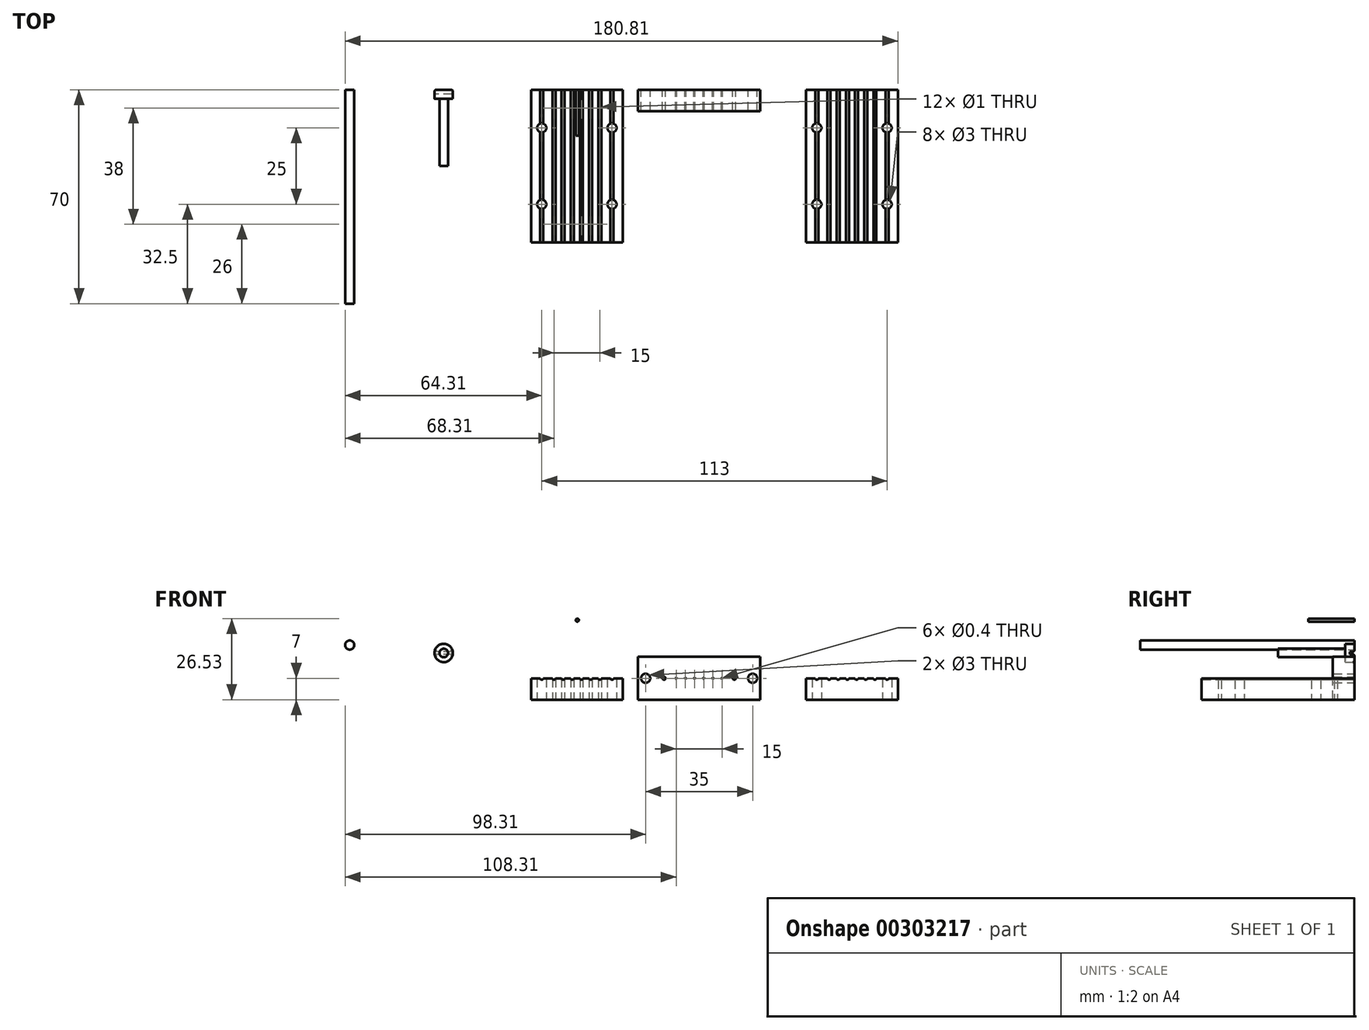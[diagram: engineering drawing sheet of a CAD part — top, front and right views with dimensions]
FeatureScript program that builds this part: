
annotation { "Feature Type Name" : "Feature", "Feature Type Description" : "" }
export const myFeature = defineFeature(function(context is Context, id is Id, definition is map)
    precondition{}
    {
        {
            var Q0;
            Q0=qCreatedBy(makeId("Front.planeOp"),FACE);
            var sketch = newSketch(context, id + "F0", { "sketchPlane" : qUnion([Q0])});
            skLineSegment(sketch, "E0.bottom", {"start": v(0, 0) * mm, "end": v(30, 0) * mm});
            skLineSegment(sketch, "E0.top", {"start": v(0, 7) * mm, "end": v(30, 7) * mm});
            skLineSegment(sketch, "E0.left", {"start": v(0, 0) * mm, "end": v(0, 7) * mm});
            skLineSegment(sketch, "E0.right", {"start": v(30, 0) * mm, "end": v(30, 7) * mm});
            skCircle(sketch, "E1", {"center": v(7.5, 7) * mm, "radius": 0.5 * mm});
            skCircle(sketch, "E2.1.0.0", {"center": v(10.5, 7) * mm, "radius": 0.5 * mm});
            skCircle(sketch, "E2.2.0.0", {"center": v(13.5, 7) * mm, "radius": 0.5 * mm});
            skCircle(sketch, "E2.3.0.0", {"center": v(16.5, 7) * mm, "radius": 0.5 * mm});
            skLineSegment(sketch, "E2.direction1", {"start": v(7.5, 7) * mm, "end": v(10.5, 7) * mm, "construction": true});
            skCircle(sketch, "E3.0.4.0", {"center": v(19.5, 7) * mm, "radius": 0.5 * mm});
            skCircle(sketch, "E3.0.5.0", {"center": v(22.5, 7) * mm, "radius": 0.5 * mm});
            skCircle(sketch, "E4", {"center": v(3.5, 7) * mm, "radius": 0.5 * mm});
            skLineSegment(sketch, "E5", {"start": v(15, 7) * mm, "end": v(15, 0) * mm, "construction": true});
            skCircle(sketch, "E6.MirrorC", {"center": v(26.5, 7) * mm, "radius": 0.5 * mm});
            skSolve(sketch);
        }
        {
            var Q0;
            Q0=makeQuery(id+"F0.imprint","IMPRINT",FACE,{"disambiguationData":[TD([[makeQuery(id+"F0.imprint","IMPRINT",EDGE,{"derivedFrom":sQuery(id+"F0.wireOp",EDGE,"E0.bottom")}),1.0]])]});
            extrude(context, id + "F1", {"entities" : qUnion([Q0]), "depth" : 50 * mm});
        }
        {
            var Q0;
            Q0=qCreatedBy(makeId("Front.planeOp"),FACE);
            var sketch = newSketch(context, id + "F2", { "sketchPlane" : qUnion([Q0])});
            skLineSegment(sketch, "E7.bottom", {"start": v(40, 0) * mm, "end": v(70, 0) * mm});
            skLineSegment(sketch, "E7.top", {"start": v(40, 7) * mm, "end": v(70, 7) * mm, "construction": true});
            skLineSegment(sketch, "E7.left", {"start": v(40, 0) * mm, "end": v(40, 7) * mm});
            skLineSegment(sketch, "E7.right", {"start": v(70, 0) * mm, "end": v(70, 7) * mm});
            skLineSegment(sketch, "E8.direction1", {"start": v(47.5, 7) * mm, "end": v(50.5, 7) * mm, "construction": true});
            skLineSegment(sketch, "E9.top", {"start": v(40, 14) * mm, "end": v(70, 14) * mm});
            skLineSegment(sketch, "E9.left", {"start": v(40, 0) * mm, "end": v(40, 14) * mm});
            skLineSegment(sketch, "E9.right", {"start": v(70, 0) * mm, "end": v(70, 14) * mm});
            skCircle(sketch, "E10", {"center": v(47.5, 7) * mm, "radius": 0.2 * mm});
            skCircle(sketch, "E11.1.0.0", {"center": v(50.5, 7) * mm, "radius": 0.2 * mm});
            skCircle(sketch, "E11.2.0.0", {"center": v(53.5, 7) * mm, "radius": 0.2 * mm});
            skCircle(sketch, "E11.3.0.0", {"center": v(56.5, 7) * mm, "radius": 0.2 * mm});
            skCircle(sketch, "E12.0.4.0", {"center": v(59.5, 7) * mm, "radius": 0.2 * mm});
            skCircle(sketch, "E12.0.5.0", {"center": v(62.5, 7) * mm, "radius": 0.2 * mm});
            skCircle(sketch, "E13", {"center": v(43.5, 7) * mm, "radius": 0.5 * mm});
            skLineSegment(sketch, "E14", {"start": v(55, 14) * mm, "end": v(55, 0) * mm, "construction": true});
            skCircle(sketch, "E15.MirrorC", {"center": v(66.5, 7) * mm, "radius": 0.5 * mm});
            skLineSegment(sketch, "E16.bottom", {"start": v(40, 0) * mm, "end": v(35, 0) * mm});
            skLineSegment(sketch, "E16.top", {"start": v(40, 14) * mm, "end": v(35, 14) * mm});
            skLineSegment(sketch, "E16.right", {"start": v(35, 0) * mm, "end": v(35, 14) * mm});
            skLineSegment(sketch, "E17", {"start": v(40, 7) * mm, "end": v(35, 7) * mm, "construction": true});
            skCircle(sketch, "E18", {"center": v(37.5, 7) * mm, "radius": 1.5 * mm});
            skLineSegment(sketch, "E19.MirrorCS", {"start": v(70, 14) * mm, "end": v(75, 14) * mm});
            skLineSegment(sketch, "E20.MirrorCS", {"start": v(75, 0) * mm, "end": v(75, 14) * mm});
            skLineSegment(sketch, "E21.MirrorCS", {"start": v(70, 0) * mm, "end": v(75, 0) * mm});
            skCircle(sketch, "E22.MirrorC", {"center": v(72.5, 7) * mm, "radius": 1.5 * mm});
            skSolve(sketch);
        }
        {
            var Q0;
            Q0=makeQuery(id+"F2.imprint","IMPRINT",FACE,{"disambiguationData":[TD([[makeQuery(id+"F2.imprint","IMPRINT",EDGE,{"derivedFrom":sQuery(id+"F2.wireOp",EDGE,"E8.3.0.0")}),1.0]])]});
            var Q1;
            Q1=makeQuery(id+"F2.imprint","IMPRINT",FACE,{"disambiguationData":[TD([[makeQuery(id+"F2.imprint","IMPRINT",EDGE,{"derivedFrom":sQuery(id+"F2.wireOp",EDGE,"E8.2.0.0")}),1.0]])]});
            var Q2;
            Q2=makeQuery(id+"F2.imprint","IMPRINT",FACE,{"disambiguationData":[TD([[makeQuery(id+"F2.imprint","IMPRINT",EDGE,{"derivedFrom":sQuery(id+"F2.wireOp",EDGE,"E8.1.0.0")}),1.0]])]});
            var Q3;
            Q3=makeQuery(id+"F2.imprint","IMPRINT",FACE,{"disambiguationData":[TD([[makeQuery(id+"F2.imprint","IMPRINT",EDGE,{"derivedFrom":sQuery(id+"F2.wireOp",EDGE,"54caae34-96a9-44bf-94f6-0ee6068eccf9")}),1.0]])]});
            var Q4;
            Q4=makeQuery(id+"F2.imprint","IMPRINT",FACE,{"disambiguationData":[TD([[makeQuery(id+"F2.imprint","IMPRINT",EDGE,{"derivedFrom":sQuery(id+"F2.wireOp",EDGE,"E12.0.4.0")}),-1.0]])]});
            var Q5;
            Q5=makeQuery(id+"F2.imprint","IMPRINT",FACE,{"disambiguationData":[TD([[makeQuery(id+"F2.imprint","IMPRINT",EDGE,{"derivedFrom":sQuery(id+"F2.wireOp",EDGE,"E12.0.5.0")}),-1.0]])]});
            var Q6;
            {var subQ0=sQuery(id+"F2.wireOp",EDGE,"E19.MirrorCS");Q6=makeQuery(id+"F2.imprint","IMPRINT",FACE,{"disambiguationData":[TD([[makeQuery(id+"F2.imprint","IMPRINT",EDGE,{"derivedFrom":subQ0}),-1.0]])]});}
            var Q7;
            {var subQ3=sQuery(id+"F2.wireOp",EDGE,"E16.bottom");Q7=makeQuery(id+"F2.imprint","IMPRINT",FACE,{"disambiguationData":[TD([[makeQuery(id+"F2.imprint","IMPRINT",EDGE,{"derivedFrom":subQ3}),-1.0]])]});}
            extrude(context, id + "F3", {"entities" : qUnion([Q0, Q1, Q2, Q3, Q4, Q5, Q6, Q7]), "depth" : 7 * mm});
        }
        {
            var Q0;
            Q0=qCreatedBy(makeId("Front.planeOp"),FACE);
            var sketch = newSketch(context, id + "F4", { "sketchPlane" : qUnion([Q0])});
            skCircle(sketch, "E23", {"center": v(-28.56, 15.28) * mm, "radius": 3 * mm});
            skCircle(sketch, "E24", {"center": v(-28.56, 15.28) * mm, "radius": 1.4 * mm});
            skSolve(sketch);
        }
        {
            var Q0;
            Q0=makeQuery(id+"F4.imprint","IMPRINT",FACE,{"disambiguationData":[TD([[makeQuery(id+"F4.imprint","IMPRINT",EDGE,{"derivedFrom":sQuery(id+"F4.wireOp",EDGE,"E23")}),1.0]])]});
            var Q1;
            Q1=makeQuery(id+"F4.imprint","IMPRINT",FACE,{"disambiguationData":[TD([[makeQuery(id+"F4.imprint","IMPRINT",EDGE,{"derivedFrom":sQuery(id+"F4.wireOp",EDGE,"E24")}),1.0]])]});
            extrude(context, id + "F5", {"entities" : qUnion([Q0, Q1]), "depth" : 3 * mm});
        }
        {
            var Q0;
            Q0=makeQuery(id+"F4.imprint","IMPRINT",FACE,{"disambiguationData":[TD([[makeQuery(id+"F4.imprint","IMPRINT",EDGE,{"derivedFrom":sQuery(id+"F4.wireOp",EDGE,"E24")}),1.0]])]});
            extrude(context, id + "F6", {"entities" : qUnion([Q0]), "operationType" : NewBodyOperationType.ADD, "depth" : 25 * mm});
        }
        {
            var Q0;
            Q0=makeQuery(id+"F4.imprint","IMPRINT",FACE,{"disambiguationData":[TD([[makeQuery(id+"F4.imprint","IMPRINT",EDGE,{"derivedFrom":sQuery(id+"F4.wireOp",EDGE,"E23")}),1.0]])]});
            var sketch = newSketch(context, id + "F7", { "sketchPlane" : qUnion([Q0])});
            skCircle(sketch, "E25.0", {"center": v(-28.56, 15.28) * mm, "radius": 1.4 * mm});
            skLineSegment(sketch, "E26.bottom", {"start": v(-24.57, 14.84) * mm, "end": v(-32.56, 14.84) * mm});
            skLineSegment(sketch, "E26.top", {"start": v(-24.57, 15.72) * mm, "end": v(-32.56, 15.72) * mm});
            skLineSegment(sketch, "E26.left", {"start": v(-24.57, 14.84) * mm, "end": v(-24.57, 15.72) * mm});
            skLineSegment(sketch, "E26.right", {"start": v(-32.56, 14.84) * mm, "end": v(-32.56, 15.72) * mm});
            skSolve(sketch);
        }
        {
            var Q0;
            {var subQ0=sQuery(id+"F7.wireOp",EDGE,"E26.top");var subQ1=sQuery(id+"F7.wireOp",EDGE,"E25.0");var subQ2=makeQuery(id+"F7.imprint","INTERSECT",VERTEX,{"disambiguationData":[OD(0.0)],"derivedFrom":[subQ1,subQ0]});Q0=makeQuery(id+"F7.imprint","IMPRINT",FACE,{"disambiguationData":[TD([[makeQuery(id+"F7.imprint","IMPRINT",EDGE,{"disambiguationData":[TD([[subQ2,-1.0]])],"derivedFrom":subQ1}),-1.0]])]});}
            var Q1;
            {var subQ0=sQuery(id+"F7.wireOp",EDGE,"E26.top");var subQ1=sQuery(id+"F7.wireOp",EDGE,"E25.0");var subQ2=makeQuery(id+"F7.imprint","INTERSECT",VERTEX,{"disambiguationData":[OD(0.0)],"derivedFrom":[subQ1,subQ0]});Q1=makeQuery(id+"F7.imprint","IMPRINT",FACE,{"disambiguationData":[TD([[makeQuery(id+"F7.imprint","IMPRINT",EDGE,{"disambiguationData":[TD([[subQ2,-1.0]])],"derivedFrom":subQ1}),1.0]])]});}
            var Q2;
            {var subQ0=sQuery(id+"F7.wireOp",EDGE,"E26.top");var subQ1=sQuery(id+"F7.wireOp",EDGE,"E25.0");var subQ2=makeQuery(id+"F7.imprint","INTERSECT",VERTEX,{"disambiguationData":[OD(1.0)],"derivedFrom":[subQ1,subQ0]});Q2=makeQuery(id+"F7.imprint","IMPRINT",FACE,{"disambiguationData":[TD([[makeQuery(id+"F7.imprint","IMPRINT",EDGE,{"disambiguationData":[TD([[subQ2,1.0]])],"derivedFrom":subQ1}),-1.0]])]});}
            extrude(context, id + "F8", {"entities" : qUnion([Q0, Q1, Q2]), "operationType" : NewBodyOperationType.REMOVE, "depth" : 1.5 * mm});
        }
        {
            var Q0;
            {var subQ0=sQuery(id+"F4.wireOp",EDGE,"E23");Q0=makeQuery(id+"F8.boolean.opBoolean","SPLIT",FACE,{"disambiguationData":[TD([makeQuery(id+"F8.opExtrude","SWEPT_FACE",FACE,{"disambiguationData":[OSD([sQuery(id+"F7.wireOp",EDGE,"E26.top")])]})])],"derivedFrom":makeQuery(id+"F5.opExtrude","CAP_FACE",FACE,{"disambiguationData":[OSD([subQ0])],"isStart":true})});}
            var Q1;
            {var subQ0=sQuery(id+"F4.wireOp",EDGE,"E23");Q1=makeQuery(id+"F8.boolean.opBoolean","SPLIT",FACE,{"disambiguationData":[TD([makeQuery(id+"F8.opExtrude","SWEPT_FACE",FACE,{"disambiguationData":[OSD([sQuery(id+"F7.wireOp",EDGE,"E26.bottom")])]})])],"derivedFrom":makeQuery(id+"F5.opExtrude","CAP_FACE",FACE,{"disambiguationData":[OSD([subQ0])],"isStart":true})});}
            fillet(context, id + "F9", {"entities" : qUnion([Q0, Q1]), "radius" : .5 * mm, "tangentPropagation" : true, "allowEdgeOverflow" : false});
        }
        {
            var Q0;
            Q0=makeQuery(id+"F1.opExtrude","SWEPT_FACE",FACE,{"disambiguationData":[OSD([sQuery(id+"F0.wireOp",EDGE,"E0.bottom")])]});
            var sketch = newSketch(context, id + "F10", { "sketchPlane" : qUnion([Q0])});
            skLineSegment(sketch, "E27", {"start": v(30, 50) * mm, "end": v(0, 0) * mm, "construction": true});
            skLineSegment(sketch, "E28.bottom", {"start": v(26.5, 37.5) * mm, "end": v(3.5, 37.5) * mm, "construction": true});
            skLineSegment(sketch, "E28.top", {"start": v(26.5, 12.5) * mm, "end": v(3.5, 12.5) * mm, "construction": true});
            skLineSegment(sketch, "E28.left", {"start": v(26.5, 37.5) * mm, "end": v(26.5, 12.5) * mm, "construction": true});
            skLineSegment(sketch, "E28.right", {"start": v(3.5, 37.5) * mm, "end": v(3.5, 12.5) * mm, "construction": true});
            skPoint(sketch, "E28.middle", {"position": v(15, 25) * mm});
            skCircle(sketch, "E29", {"center": v(3.5, 12.5) * mm, "radius": 1.5 * mm});
            skCircle(sketch, "E30.0.1.0", {"center": v(3.5, 37.5) * mm, "radius": 1.5 * mm});
            skCircle(sketch, "E30.1.0.0", {"center": v(26.5, 12.5) * mm, "radius": 1.5 * mm});
            skCircle(sketch, "E30.1.1.0", {"center": v(26.5, 37.5) * mm, "radius": 1.5 * mm});
            skLineSegment(sketch, "E30.direction1", {"start": v(3.5, 12.5) * mm, "end": v(26.5, 12.5) * mm, "construction": true});
            skLineSegment(sketch, "E30.direction2", {"start": v(3.5, 12.5) * mm, "end": v(3.5, 37.5) * mm, "construction": true});
            skLineSegment(sketch, "E31.bottom", {"start": v(22.5, 44) * mm, "end": v(7.5, 44) * mm, "construction": true});
            skLineSegment(sketch, "E31.top", {"start": v(22.5, 6) * mm, "end": v(7.5, 6) * mm, "construction": true});
            skLineSegment(sketch, "E31.left", {"start": v(22.5, 44) * mm, "end": v(22.5, 6) * mm, "construction": true});
            skLineSegment(sketch, "E31.right", {"start": v(7.5, 44) * mm, "end": v(7.5, 6) * mm, "construction": true});
            skCircle(sketch, "E32", {"center": v(7.5, 6) * mm, "radius": 0.5 * mm});
            skCircle(sketch, "E33.0.1.0", {"center": v(7.5, 44) * mm, "radius": 0.5 * mm});
            skCircle(sketch, "E33.1.0.0", {"center": v(10.5, 6) * mm, "radius": 0.5 * mm});
            skCircle(sketch, "E33.1.1.0", {"center": v(10.5, 44) * mm, "radius": 0.5 * mm});
            skCircle(sketch, "E33.2.0.0", {"center": v(13.5, 6) * mm, "radius": 0.5 * mm});
            skCircle(sketch, "E33.2.1.0", {"center": v(13.5, 44) * mm, "radius": 0.5 * mm});
            skCircle(sketch, "E33.3.0.0", {"center": v(16.5, 6) * mm, "radius": 0.5 * mm});
            skCircle(sketch, "E33.3.1.0", {"center": v(16.5, 44) * mm, "radius": 0.5 * mm});
            skLineSegment(sketch, "E33.direction1", {"start": v(7.5, 6) * mm, "end": v(10.5, 6) * mm, "construction": true});
            skLineSegment(sketch, "E33.direction2", {"start": v(7.5, 6) * mm, "end": v(7.5, 44) * mm, "construction": true});
            skCircle(sketch, "E34.0.4.0", {"center": v(19.5, 6) * mm, "radius": 0.5 * mm});
            skCircle(sketch, "E34.0.4.1", {"center": v(19.5, 44) * mm, "radius": 0.5 * mm});
            skCircle(sketch, "E34.0.5.0", {"center": v(22.5, 6) * mm, "radius": 0.5 * mm});
            skCircle(sketch, "E34.0.5.1", {"center": v(22.5, 44) * mm, "radius": 0.5 * mm});
            skSolve(sketch);
        }
        {
            var Q0;
            Q0=makeQuery(id+"F1.opExtrude","SWEPT_BODY",BODY,{"disambiguationData":[OSD([sQuery(id+"F0.wireOp",EDGE,"E0.bottom"),sQuery(id+"F0.wireOp",EDGE,"E0.top"),sQuery(id+"F0.wireOp",EDGE,"E0.left"),sQuery(id+"F0.wireOp",EDGE,"E0.right"),sQuery(id+"F0.wireOp",EDGE,"E1"),sQuery(id+"F0.wireOp",EDGE,"E2.1.0.0"),sQuery(id+"F0.wireOp",EDGE,"E2.2.0.0"),sQuery(id+"F0.wireOp",EDGE,"E2.3.0.0")])]});
            transform(context, id + "F11", {"entities" : qUnion([Q0]), "transformType" : TransformType.TRANSLATION_3D, "dx" : 90 * mm, "dy" : 0 * mm, "dz" : 0 * mm, "makeCopy" : true});
        }
        {
            var Q0;
            Q0=qSketchRegion(id+"F10",true);
            extrude(context, id + "F12", {"entities" : qUnion([Q0]), "operationType" : NewBodyOperationType.REMOVE, "oppositeDirection" : true, "depth" : 25 * mm});
        }
        {
            var Q0;
            Q0=makeQuery(id+"F11.opPattern","COPY",FACE,{"derivedFrom":makeQuery(id+"F1.opExtrude","SWEPT_FACE",FACE,{"disambiguationData":[OSD([sQuery(id+"F0.wireOp",EDGE,"E0.bottom")])]}),"instanceName":"1"});
            var sketch = newSketch(context, id + "F13", { "sketchPlane" : qUnion([Q0])});
            skLineSegment(sketch, "E35", {"start": v(90, 0) * mm, "end": v(120, 50) * mm, "construction": true});
            skLineSegment(sketch, "E36.bottom", {"start": v(93.5, 12.5) * mm, "end": v(116.5, 12.5) * mm, "construction": true});
            skLineSegment(sketch, "E36.top", {"start": v(93.5, 37.5) * mm, "end": v(116.5, 37.5) * mm, "construction": true});
            skLineSegment(sketch, "E36.left", {"start": v(93.5, 12.5) * mm, "end": v(93.5, 37.5) * mm, "construction": true});
            skLineSegment(sketch, "E36.right", {"start": v(116.5, 12.5) * mm, "end": v(116.5, 37.5) * mm, "construction": true});
            skPoint(sketch, "E36.middle", {"position": v(105, 25) * mm});
            skCircle(sketch, "E37", {"center": v(116.5, 37.5) * mm, "radius": 1.5 * mm});
            skCircle(sketch, "E38.0.1.0", {"center": v(116.5, 12.5) * mm, "radius": 1.5 * mm});
            skCircle(sketch, "E38.1.0.0", {"center": v(93.5, 37.5) * mm, "radius": 1.5 * mm});
            skCircle(sketch, "E38.1.1.0", {"center": v(93.5, 12.5) * mm, "radius": 1.5 * mm});
            skLineSegment(sketch, "E38.direction1", {"start": v(116.5, 37.5) * mm, "end": v(93.5, 37.5) * mm, "construction": true});
            skLineSegment(sketch, "E38.direction2", {"start": v(116.5, 37.5) * mm, "end": v(116.5, 12.5) * mm, "construction": true});
            skSolve(sketch);
        }
        {
            var Q0;
            Q0=qSketchRegion(id+"F13",true);
            extrude(context, id + "F14", {"entities" : qUnion([Q0]), "operationType" : NewBodyOperationType.REMOVE, "oppositeDirection" : true, "depth" : 25 * mm});
        }
        {
            var Q0;
            Q0=qCreatedBy(makeId("Front.planeOp"),FACE);
            var sketch = newSketch(context, id + "F15", { "sketchPlane" : qUnion([Q0])});
            skCircle(sketch, "E39", {"center": v(15.15, 26.03) * mm, "radius": 0.5 * mm});
            skSolve(sketch);
        }
        {
            var Q0;
            Q0=makeQuery(id+"F15.imprint","IMPRINT",FACE,{"disambiguationData":[TD([[makeQuery(id+"F15.imprint","IMPRINT",EDGE,{"derivedFrom":sQuery(id+"F15.wireOp",EDGE,"E39")}),1.0]])]});
            extrude(context, id + "F16", {"entities" : qUnion([Q0]), "depth" : 15 * mm});
        }
        {
            var Q0;
            Q0=qCreatedBy(makeId("Front.planeOp"),FACE);
            var sketch = newSketch(context, id + "F17", { "sketchPlane" : qUnion([Q0])});
            skCircle(sketch, "E40", {"center": v(-59.31, 17.88) * mm, "radius": 1.5 * mm});
            skSolve(sketch);
        }
        {
            var Q0;
            Q0=makeQuery(id+"F17.imprint","IMPRINT",FACE,{"disambiguationData":[TD([[makeQuery(id+"F17.imprint","IMPRINT",EDGE,{"derivedFrom":sQuery(id+"F17.wireOp",EDGE,"E40")}),1.0]])]});
            extrude(context, id + "F18", {"entities" : qUnion([Q0]), "depth" : 70 * mm});
        }
    });
